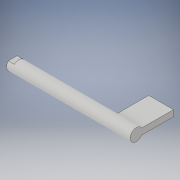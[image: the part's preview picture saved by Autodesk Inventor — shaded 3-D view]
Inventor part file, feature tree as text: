
AUTODESK INVENTOR PART (.ipt)
format: ipt  version: 2017 (Build 210142000, 142)  size: 119,808 bytes
history: native  units: in
note: dims shown in document units (in); Inventor stores cm internally (conversion verified against a paired STEP export)
features: extrude x3, sketch x3, projected_geometry x2
ambient origin geometry x8: Origin, YZ Plane, XZ Plane, XY Plane, X Axis, Y Axis, Z Axis, Center Point
bodies: Solid1 (feature_tree)
feature tree (8):
  extrude  "Extrusion1"  Depth=5.0in TaperAngle=0.0deg
  extrude  "Extrusion2"  Depth=0.25in
  extrude  "Extrusion3"  Depth=0.25in
  sketch  "Sketch1"  dims[d0=0.5in d1=5.0in d2=0.0in]
  sketch  "Sketch2"  dims[d3=0.5in d4=0.25in]
  projected_geometry  "Projected Loop1"
  sketch  "Sketch3"  dims[d5=0.125in d6=1.5in d7=0.0in d8=1.0in d9=0.0in d10=0.175in d11=0.25in d12=0.0in]
  projected_geometry  "Projected Loop2"
